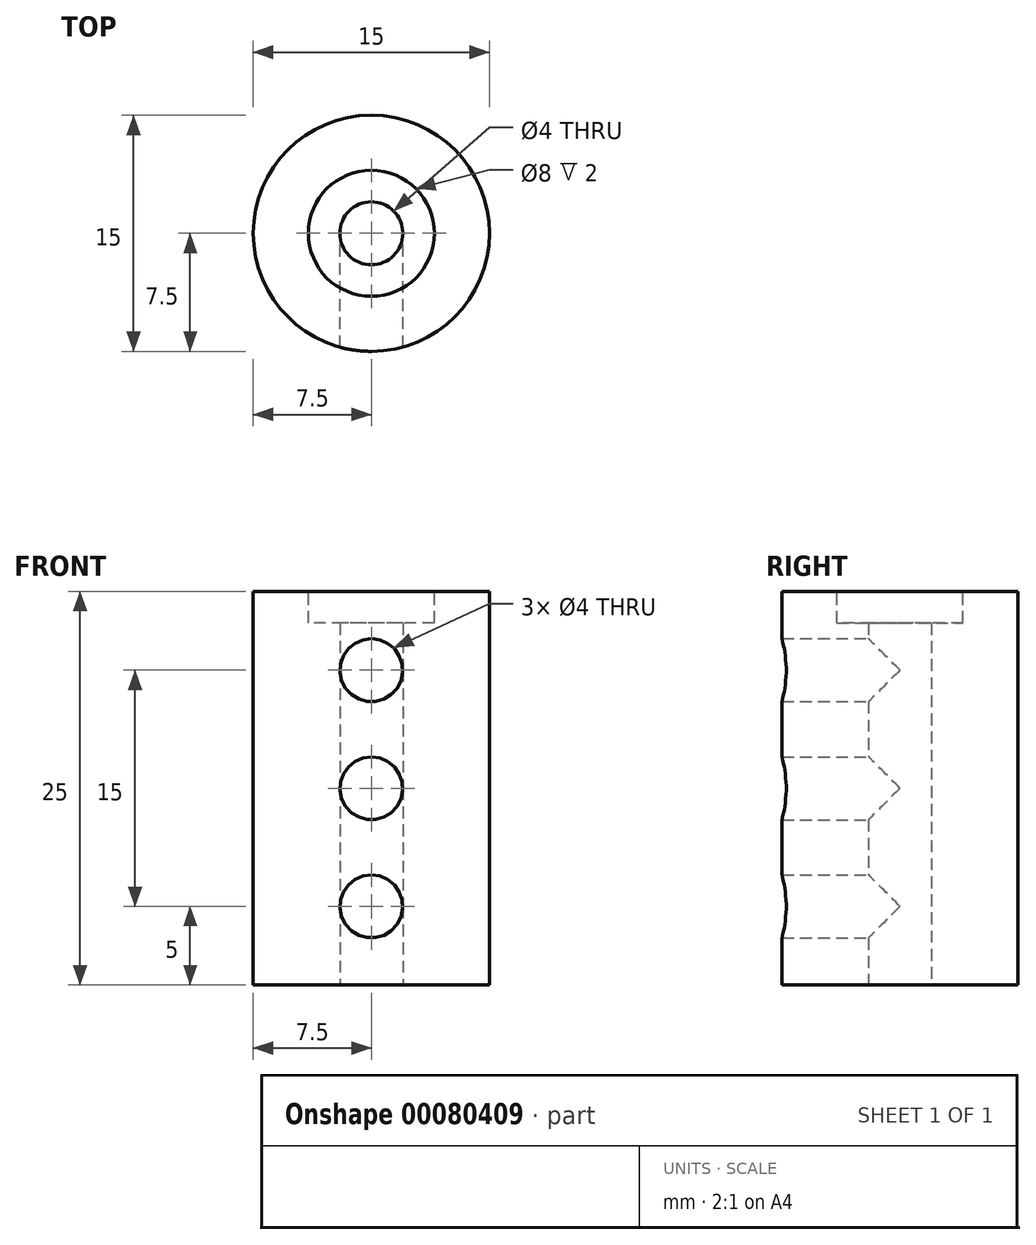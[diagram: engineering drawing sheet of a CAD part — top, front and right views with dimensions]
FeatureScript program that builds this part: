
annotation { "Feature Type Name" : "Feature", "Feature Type Description" : "" }
export const myFeature = defineFeature(function(context is Context, id is Id, definition is map)
    precondition{}
    {
        {
            var Q0;
            Q0=qCreatedBy(makeId("Top.planeOp"),FACE);
            var sketch = newSketch(context, id + "F0", { "sketchPlane" : qUnion([Q0])});
            skCircle(sketch, "E0", {"center": v(0, 0) * mm, "radius": 7.5 * mm});
            skCircle(sketch, "E1", {"center": v(0, 0) * mm, "radius": 2 * mm});
            skSolve(sketch);
        }
        {
            var Q0;
            Q0 = qSketchRegion(id + "F0", true);
            extrude(context, id + "F1", {"entities" : qUnion([Q0]), "endBound" : BoundingType.SYMMETRIC, "depth" : 25 * mm});
        }
        {
            var Q0;
            Q0=qCreatedBy(makeId("Front.planeOp"),FACE);
            var sketch = newSketch(context, id + "F2", { "sketchPlane" : qUnion([Q0])});
            skCircle(sketch, "E2", {"center": v(0, 7.5) * mm, "radius": 2 * mm});
            skCircle(sketch, "E3.MirrorC", {"center": v(0, -7.5) * mm, "radius": 2 * mm});
            skCircle(sketch, "E4", {"center": v(0, 0) * mm, "radius": 2 * mm});
            skSolve(sketch);
        }
        {
            var Q0;
            Q0 = qSketchRegion(id + "F2", true);
            extrude(context, id + "F3", {"entities" : qUnion([Q0]), "operationType" : NewBodyOperationType.REMOVE, "depth" : 25 * mm});
        }
        {
            var Q0;
            Q0=makeQuery(id+"F1.opExtrude","CAP_FACE",FACE,{"disambiguationData":[OSD([sQuery(id+"F0.wireOp",EDGE,"E0"),sQuery(id+"F0.wireOp",EDGE,"E1")])],"isStart":false});
            var sketch = newSketch(context, id + "F4", { "sketchPlane" : qUnion([Q0])});
            skCircle(sketch, "E5", {"center": v(0, 0) * mm, "radius": 4 * mm});
            skSolve(sketch);
        }
        {
            var Q0;
            Q0 = qSketchRegion(id + "F4", true);
            extrude(context, id + "F5", {"entities" : qUnion([Q0]), "operationType" : NewBodyOperationType.REMOVE, "oppositeDirection" : true, "depth" : 2 * mm});
        }
    });
